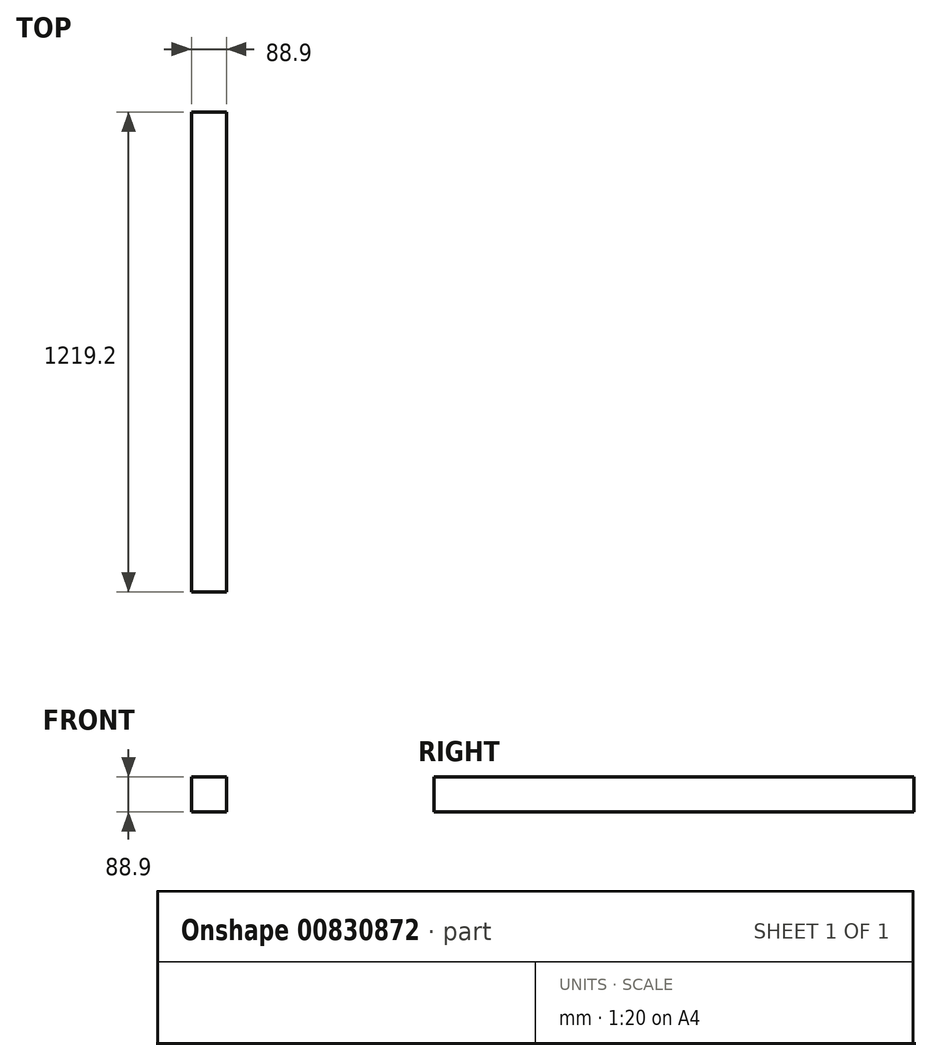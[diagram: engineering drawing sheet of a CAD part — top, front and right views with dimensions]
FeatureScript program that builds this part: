
annotation { "Feature Type Name" : "Feature", "Feature Type Description" : "" }
export const myFeature = defineFeature(function(context is Context, id is Id, definition is map)
    precondition{}
    {
        {
            var Q0;
            Q0=qCreatedBy(makeId("Front.planeOp"),FACE);
            var sketch = newSketch(context, id + "F0", { "sketchPlane" : qUnion([Q0])});
            skLineSegment(sketch, "E0.bottom", {"start": v(-44.45, 44.45) * mm, "end": v(44.45, 44.45) * mm});
            skLineSegment(sketch, "E0.top", {"start": v(-44.45, -44.45) * mm, "end": v(44.45, -44.45) * mm});
            skLineSegment(sketch, "E0.left", {"start": v(-44.45, 44.45) * mm, "end": v(-44.45, -44.45) * mm});
            skLineSegment(sketch, "E0.right", {"start": v(44.45, 44.45) * mm, "end": v(44.45, -44.45) * mm});
            skPoint(sketch, "E0.middle", {"position": v(0, 0) * mm});
            skSolve(sketch);
        }
        {
            var Q0;
            Q0=makeQuery(id+"F0.imprint","IMPRINT",FACE,{"disambiguationData":[TD([[makeQuery(id+"F0.imprint","IMPRINT",EDGE,{"derivedFrom":sQuery(id+"F0.wireOp",EDGE,"E0.bottom")}),-1.0]])]});
            extrude(context, id + "F1", {"entities" : qUnion([Q0]), "endBound" : BoundingType.SYMMETRIC, "depth" : 1219.2 * mm, "offsetDistance" : 25.4 * mm});
        }
    });
